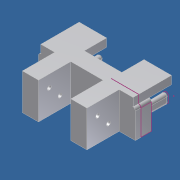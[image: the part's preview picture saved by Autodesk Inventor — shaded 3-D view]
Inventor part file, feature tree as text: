
AUTODESK INVENTOR PART (.ipt)
format: ipt  version: unknown  size: 377,344 bytes
history: native  units: in
note: dims shown in document units (in); Inventor stores cm internally (conversion verified against a paired STEP export)
features: other x20, sketch x14, extrude x11, fillet x1, mirror x1
ambient origin geometry x8: Origin, YZ Plane, XZ Plane, XY Plane, X Axis, Y Axis, Z Axis, Center Point
bodies: Solid2 (feature_tree)
feature tree (47):
  sketch  "Sketch1"  dims[d15=0.1437in d18=0.69in d19=-0.0069in]
  extrude  "Extrusion2"  Depth=0.69in
  extrude  "Extrusion3"  Depth=0.25in
  extrude  "Extrusion4"  Depth=0.06in
  sketch  "Sketch4"  dims[d35=0.174in d36=0.0in d37=0.25in d38=0.0in]
  fillet  "Fillet1"  Radius=0.076in
  extrude  "Extrusion5"  Depth=0.25in TaperAngle=0.0deg
  sketch  "Sketch7"  dims[d42=1.0in d43=0.0in d44=0.25in]
  sketch  "Sketch8"  dims[d45=1.0in d46=0.0in d52=0.125in]
  extrude  "Extrusion6"  Depth=0.25in
  extrude  "Extrusion7"  Depth=0.25in
  extrude  "Extrusion8"  Depth=0.125in
  extrude  "Extrusion9"  Depth=1.0in TaperAngle=0.0deg
  extrude  "Extrusion10"  Depth=0.5in TaperAngle=0.0deg
  extrude  "Extrusion11"  [1 undecoded]
  extrude  "Extrusion12"  [1 undecoded]
  mirror  "Mirror1"
  sketch  "Sketch2"  dims[d25=0.25in d26=0.0in d27=0.25in]
  sketch  "Sketch3"  dims[d28=0.94in d29=0.0in d30=0.06in d31=0.076in d32=0.0in]
  sketch  "Sketch5"  dims[d39=0.25in d40=0.0in d41=0.25in]
  sketch  "Sketch9"  dims[d53=0.125in d54=1.0in d55=0.0in]
  sketch  "Sketch10"  dims[d56=0.5in d57=0.5in d58=0.0in]
  sketch  "Sketch11"
  sketch  "Sketch12"
  sketch  "Sketch13"
  sketch  "Sketch14"
  sketch  "Sketch16"
  other  "Composite1"
  other  "Composite2"
  other  "Composite3"
  other  "Composite4"
  other  "Composite5"
  other  "Composite6"
  other  "Composite7"
  other  "Composite8"
  other  "Composite9"
  other  "Composite10"
  other  "Srf1"
  other  "Srf2"
  other  "Srf3"
  other  "Srf4"
  other  "Srf5"
  other  "Srf6"
  other  "Srf7"
  other  "Srf8"
  other  "Srf9"
  other  "Srf10"
note: 2 required parameter values undecoded (feature->parameter linkage not recoverable at this tier; creation-order binding heuristic only, values carry confidence <= 0.55)
